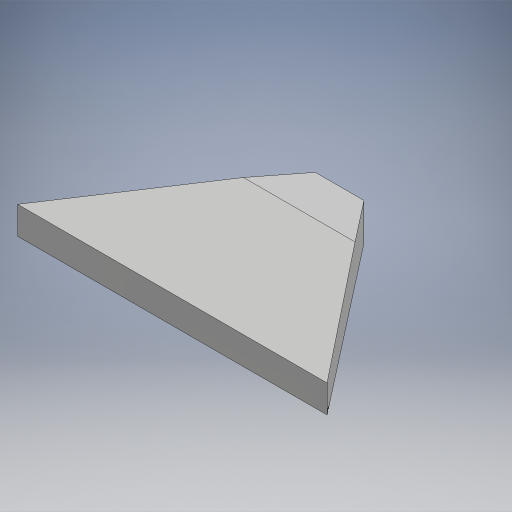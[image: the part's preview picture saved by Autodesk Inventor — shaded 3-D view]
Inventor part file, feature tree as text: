
AUTODESK INVENTOR PART (.ipt)
format: ipt  version: 2023.2 (Build 272271000, 271)  size: 271,872 bytes
history: native  units: in
note: dims shown in document units (in); Inventor stores cm internally (conversion verified against a paired STEP export)
features: extrude x1, sketch x1
ambient origin geometry x8: Origin, YZ Plane, XZ Plane, XY Plane, X Axis, Y Axis, Z Axis, Center Point
bodies: Solid1 (feature_tree)
feature tree (2):
  extrude  "Extrusion1"  Depth=0.25in
  sketch  "Sketch2"  dims[d3=0.375in d4=0.25in d5=0.25in d6=0.0in]
